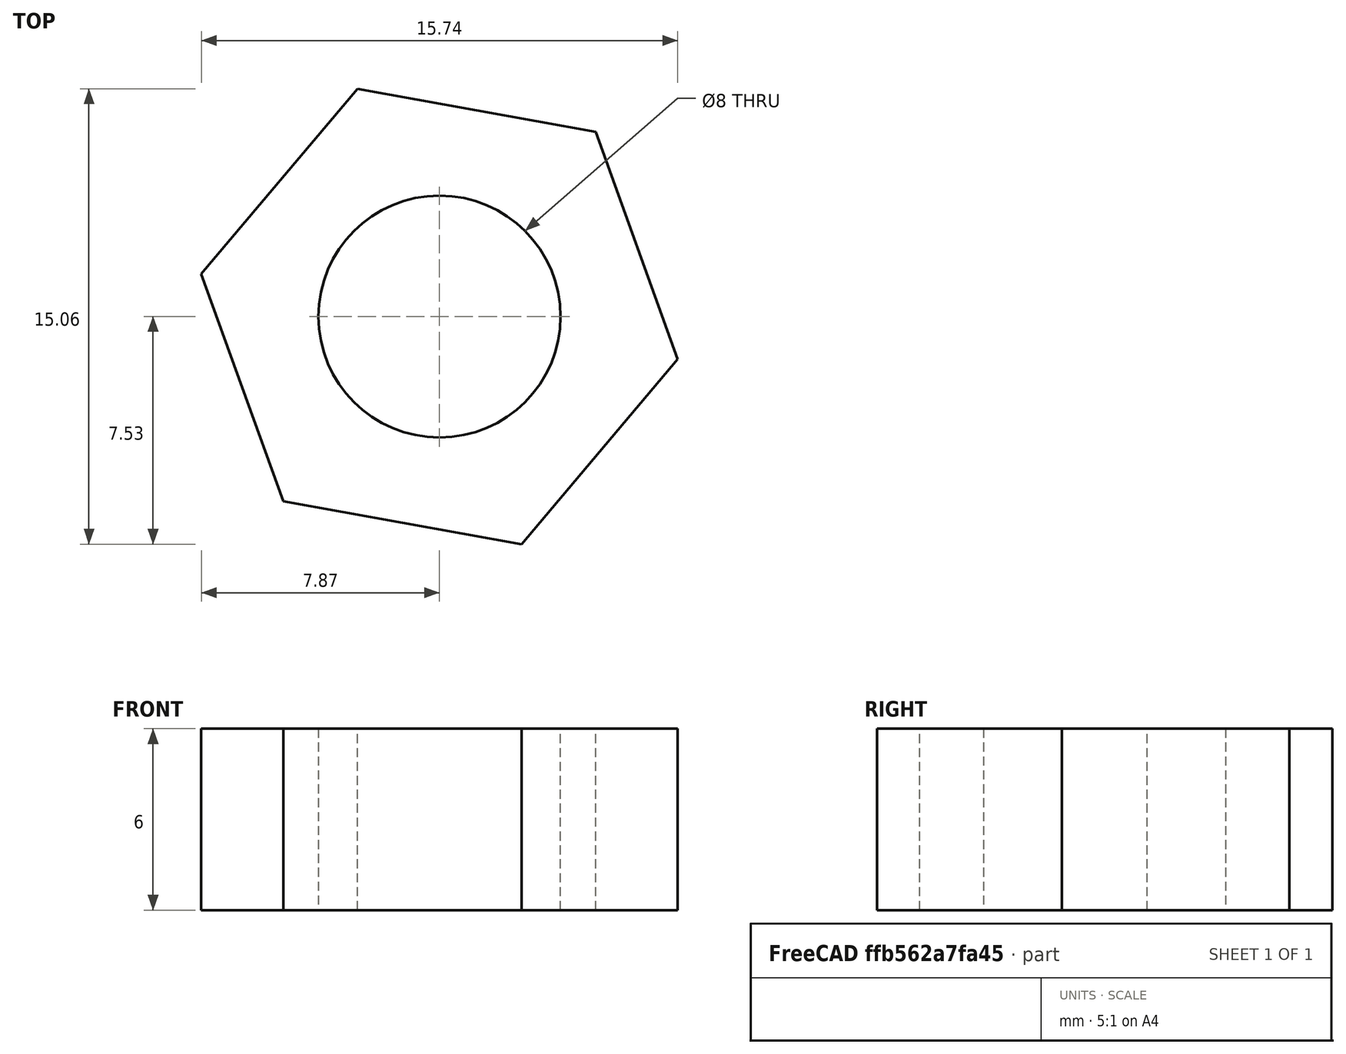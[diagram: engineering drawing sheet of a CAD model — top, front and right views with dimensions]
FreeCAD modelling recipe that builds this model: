
FCSTD DOCUMENT  (FreeCAD 0.19R24276 (Git))
Label: gaika_M8_v1
License: All rights reserved
LicenseURL: http://en.wikipedia.org/wiki/All_rights_reserved
objects: Sketcher::SketchObject×1, PartDesign::Pad×1, PartDesign::Body×1
note: 4 computed .brp shape members not serialized (recipe doc carries the construction recipe); baked Part::Feature solids carry a one-line shape summary decoded from their .brp

FEATURE [Sketcher::SketchObject] Sketch
  FullyConstrained = false
  MapMode = 5
  Support = -> [XY_Plane]
  sketch-geometry (8):
    g0: LineSegment StartX=5.16082 StartY=6.11276 StartZ=0 EndX=-2.7134 EndY=7.52579 EndZ=0
    g1: LineSegment StartX=-2.7134 StartY=7.52579 StartZ=0 EndX=-7.87422 EndY=1.41302 EndZ=0
    g2: LineSegment StartX=-7.87422 StartY=1.41302 StartZ=0 EndX=-5.16082 EndY=-6.11276 EndZ=0
    g3: LineSegment StartX=-5.16082 StartY=-6.11276 StartZ=0 EndX=2.7134 EndY=-7.52579 EndZ=0
    g4: LineSegment StartX=2.7134 StartY=-7.52579 StartZ=0 EndX=7.87422 EndY=-1.41302 EndZ=0
    g5: LineSegment StartX=7.87422 StartY=-1.41302 StartZ=0 EndX=5.16082 EndY=6.11276 EndZ=0
    g6: Circle CenterX=0 CenterY=0 CenterZ=0 NormalX=0 NormalY=0 NormalZ=1 AngleXU=0 Radius=8
    g7: Circle CenterX=0 CenterY=0 CenterZ=0 NormalX=0 NormalY=0 NormalZ=1 AngleXU=0 Radius=4
  constraints (17):
    c: Coincident(g0,g1)
    c: Coincident(g1,g2)
    c: Coincident(g2,g3)
    c: Coincident(g3,g4)
    c: Coincident(g4,g5)
    c: Coincident(g5,g0)
    c: Equal(g0, g1-g5) x5
    c: PointOnObject(g0,g6)
    c: PointOnObject(g1,g6)
    c: PointOnObject(g2,g6)
    c: PointOnObject(g3,g6)
    c: PointOnObject(g4,g6)
    c: PointOnObject(g5,g6)
    c: Coincident(g6,g-1)
    c: Coincident(g7,g-1)
    c: Diameter(g7) = 8
    c: Distance(g1) = 8
FEATURE [PartDesign::Pad] Pad
  Direction = (1,1,1)
  Length = 6
  Length2 = 100
  Profile = -> Sketch
  Type = 0
FEATURE [PartDesign::Body] Body
  Group = -> [Sketch,Pad]
  Origin = -> Origin
  Tip = -> Pad
